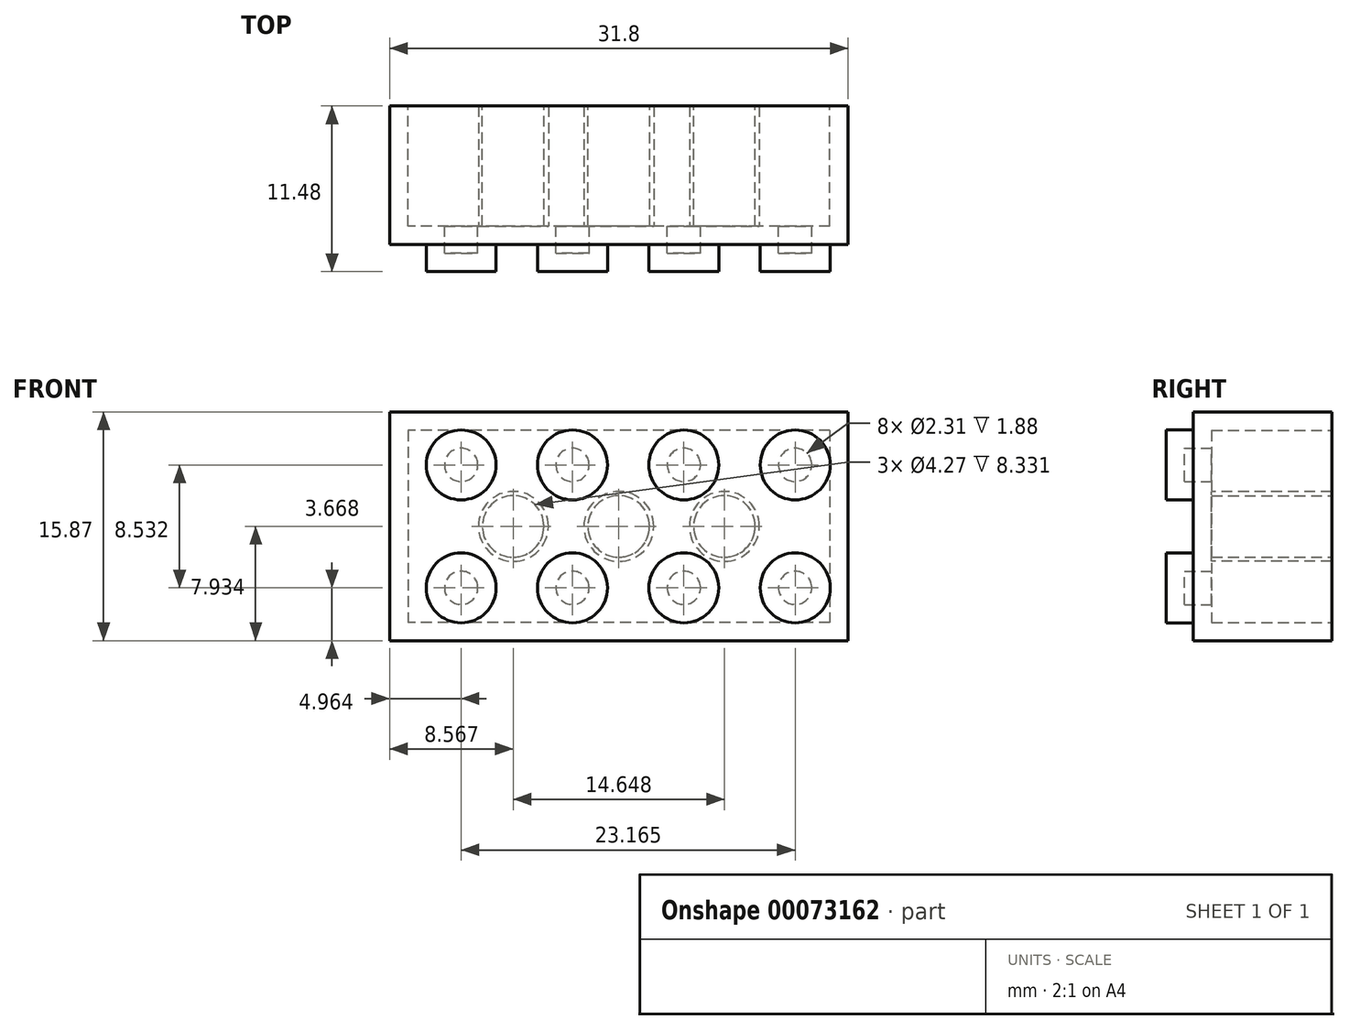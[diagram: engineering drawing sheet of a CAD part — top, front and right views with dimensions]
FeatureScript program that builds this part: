
annotation { "Feature Type Name" : "Feature", "Feature Type Description" : "" }
export const myFeature = defineFeature(function(context is Context, id is Id, definition is map)
    precondition{}
    {
        {
            var Q0;
            Q0=qCreatedBy(makeId("Front.planeOp"),FACE);
            var sketch = newSketch(context, id + "F0", { "sketchPlane" : qUnion([Q0])});
            skLineSegment(sketch, "E0.bottom", {"start": v(14.37, 4.37) * mm, "end": v(-17.43, 4.37) * mm});
            skLineSegment(sketch, "E0.top", {"start": v(14.37, -11.5) * mm, "end": v(-17.43, -11.5) * mm});
            skLineSegment(sketch, "E0.left", {"start": v(14.37, 4.37) * mm, "end": v(14.37, -11.5) * mm});
            skLineSegment(sketch, "E0.right", {"start": v(-17.43, 4.37) * mm, "end": v(-17.43, -11.5) * mm});
            skSolve(sketch);
        }
        {
            var Q0;
            Q0 = qSketchRegion(id + "F0", true);
            extrude(context, id + "F1", {"entities" : qUnion([Q0]), "depth" : 9.6 * mm});
        }
        {
            var Q0;
            Q0=makeQuery(id+"F1.opExtrude","CAP_FACE",FACE,{"disambiguationData":[OSD([sQuery(id+"F0.wireOp",EDGE,"E0.bottom"),sQuery(id+"F0.wireOp",EDGE,"E0.top"),sQuery(id+"F0.wireOp",EDGE,"E0.left"),sQuery(id+"F0.wireOp",EDGE,"E0.right")])],"isStart":false});
            var sketch = newSketch(context, id + "F2", { "sketchPlane" : qUnion([Q0])});
            skCircle(sketch, "E1", {"center": v(10.7, -7.83) * mm, "radius": 2.43 * mm});
            skLineSegment(sketch, "E2.1", {"start": v(14.37, 4.37) * mm, "end": v(14.37, -11.5) * mm});
            skLineSegment(sketch, "E3.0", {"start": v(14.37, -11.5) * mm, "end": v(-17.43, -11.5) * mm});
            skLineSegment(sketch, "E4.0", {"start": v(14.37, 4.37) * mm, "end": v(-17.43, 4.37) * mm});
            skLineSegment(sketch, "E5", {"start": v(14.37, -3.57) * mm, "end": v(-17.43, -3.57) * mm, "construction": true});
            skCircle(sketch, "E6.1.0.0", {"center": v(2.98, -7.83) * mm, "radius": 2.43 * mm});
            skCircle(sketch, "E6.2.0.0", {"center": v(-4.74, -7.83) * mm, "radius": 2.43 * mm});
            skCircle(sketch, "E6.3.0.0", {"center": v(-12.47, -7.83) * mm, "radius": 2.43 * mm});
            skLineSegment(sketch, "E6.direction1", {"start": v(10.7, -7.83) * mm, "end": v(2.98, -7.83) * mm, "construction": true});
            skCircle(sketch, "E7.MirrorC", {"center": v(2.98, 0.7) * mm, "radius": 2.43 * mm});
            skCircle(sketch, "E8.MirrorC", {"center": v(-4.74, 0.7) * mm, "radius": 2.43 * mm});
            skCircle(sketch, "E9.MirrorC", {"center": v(-12.47, 0.7) * mm, "radius": 2.43 * mm});
            skCircle(sketch, "E10.MirrorC", {"center": v(10.7, 0.7) * mm, "radius": 2.43 * mm});
            skSolve(sketch);
        }
        {
            var Q0;
            Q0 = qSketchRegion(id + "F2", true);
            extrude(context, id + "F3", {"entities" : qUnion([Q0]), "operationType" : NewBodyOperationType.ADD, "depth" : 1.88 * mm});
        }
        {
            var Q0;
            Q0=makeQuery(id+"F1.opExtrude","CAP_FACE",FACE,{"disambiguationData":[OSD([sQuery(id+"F0.wireOp",EDGE,"E0.bottom"),sQuery(id+"F0.wireOp",EDGE,"E0.top"),sQuery(id+"F0.wireOp",EDGE,"E0.left"),sQuery(id+"F0.wireOp",EDGE,"E0.right")])],"isStart":true});
            shell(context, id + "F4", {"entities" : qUnion([Q0]), "thickness" : 1.27 * mm});
        }
        {
            var Q0;
            Q0=makeQuery(id+"F4.opShell","OFFSET_FACE",FACE,{"disambiguationData":[OSD([sQuery(id+"F0.wireOp",EDGE,"E0.bottom"),sQuery(id+"F0.wireOp",EDGE,"E0.top"),sQuery(id+"F0.wireOp",EDGE,"E0.left"),sQuery(id+"F0.wireOp",EDGE,"E0.right")])]});
            var sketch = newSketch(context, id + "F5", { "sketchPlane" : qUnion([Q0])});
            skCircle(sketch, "E11", {"center": v(1.53, -3.57) * mm, "radius": 2.43 * mm});
            skPoint(sketch, "E12", {"position": v(16.16, -3.57) * mm});
            skLineSegment(sketch, "E13", {"start": v(1.53, -10.23) * mm, "end": v(1.53, 3.1) * mm, "construction": true});
            skLineSegment(sketch, "E14", {"start": v(1.53, -3.57) * mm, "end": v(16.16, -3.57) * mm, "construction": true});
            skCircle(sketch, "E15", {"center": v(8.85, -3.57) * mm, "radius": 2.43 * mm});
            skCircle(sketch, "E16.MirrorC", {"center": v(-5.79, -3.57) * mm, "radius": 2.43 * mm});
            skSolve(sketch);
        }
        {
            var Q0;
            Q0 = qSketchRegion(id + "F5", true);
            var Q1;
            Q1=makeQuery(id+"F1.opExtrude","CAP_FACE",FACE,{"disambiguationData":[OSD([sQuery(id+"F0.wireOp",EDGE,"E0.bottom"),sQuery(id+"F0.wireOp",EDGE,"E0.top"),sQuery(id+"F0.wireOp",EDGE,"E0.left"),sQuery(id+"F0.wireOp",EDGE,"E0.right")])],"isStart":true});
            extrude(context, id + "F6", {"entities" : qUnion([Q0]), "operationType" : NewBodyOperationType.ADD, "endBound" : BoundingType.UP_TO_SURFACE, "endBoundEntityFace" : qUnion([Q1]), "depth" : 25.4 * mm});
        }
        {
            var Q0;
            Q0=makeQuery(id+"F6.opExtrude","CAP_FACE",FACE,{"disambiguationData":[OSD([sQuery(id+"F5.wireOp",EDGE,"E15")])],"isStart":false});
            var sketch = newSketch(context, id + "F7", { "sketchPlane" : qUnion([Q0])});
            skCircle(sketch, "E17", {"center": v(-5.79, -3.57) * mm, "radius": 2.14 * mm});
            skCircle(sketch, "E18.1.0.0", {"center": v(1.54, -3.57) * mm, "radius": 2.14 * mm});
            skCircle(sketch, "E18.2.0.0", {"center": v(8.86, -3.57) * mm, "radius": 2.14 * mm});
            skLineSegment(sketch, "E18.direction1", {"start": v(-5.79, -3.57) * mm, "end": v(1.54, -3.57) * mm, "construction": true});
            skSolve(sketch);
        }
        {
            var Q0;
            Q0 = qSketchRegion(id + "F7", true);
            var Q1;
            Q1=makeQuery(id+"F4.opShell","OFFSET_FACE",FACE,{"disambiguationData":[OSD([sQuery(id+"F0.wireOp",EDGE,"E0.bottom"),sQuery(id+"F0.wireOp",EDGE,"E0.top"),sQuery(id+"F0.wireOp",EDGE,"E0.left"),sQuery(id+"F0.wireOp",EDGE,"E0.right")])]});
            extrude(context, id + "F8", {"entities" : qUnion([Q0]), "operationType" : NewBodyOperationType.REMOVE, "endBound" : BoundingType.UP_TO_SURFACE, "oppositeDirection" : true, "endBoundEntityFace" : qUnion([Q1]), "depth" : 25.4 * mm});
        }
    });
